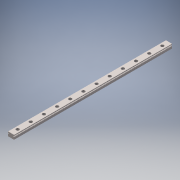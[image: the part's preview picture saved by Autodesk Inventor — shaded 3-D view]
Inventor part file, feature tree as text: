
AUTODESK INVENTOR PART (.ipt)
format: ipt  version: 2018 (Build 220112000, 112)  size: 164,352 bytes
history: native  units: in
note: dims shown in document units (in); Inventor stores cm internally (conversion verified against a paired STEP export)
features: other x1, extrude x1, plane x1, sketch x1
ambient origin geometry x8: Origin, YZ Plane, XZ Plane, XY Plane, X Axis, Y Axis, Z Axis, Center Point
bodies: Solid1 (feature_tree)
feature tree (4):
  other  "Pattern1"
  extrude  "Extrusion1"  Depth=0.7874in
  plane  "Work Plane1"
  sketch  "Sketch1"  dims[d0=3.937in d1=0.7874in d2=0.3937in d3=0.0in]
